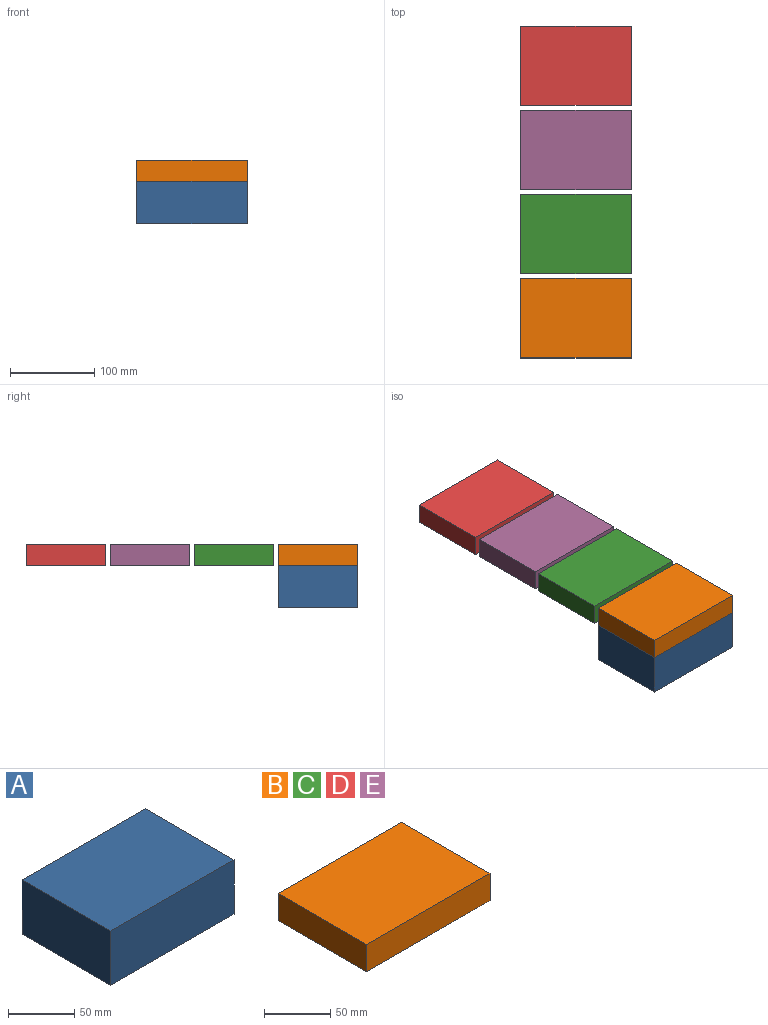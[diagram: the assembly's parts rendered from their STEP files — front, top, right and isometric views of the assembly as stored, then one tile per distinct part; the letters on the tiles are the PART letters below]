
ASSEMBLY  parts=5 mates=1
PART A: 6 faces, bbox 131.2x94.4x50 mm
  f0: plane 131.18x50mm, normal (0,-1,0), area 6559.2mm2, adj f1,f3,f4,f5
  f1: plane 94.37x50mm, normal (1,0,0), area 4718.6mm2, adj f0,f2,f4,f5
  f2: plane 131.18x50mm, normal (0,1,0), area 6559.2mm2, adj f1,f3,f4,f5
  f3: plane 94.37x50mm, normal (-1,0,0), area 4718.6mm2, adj f0,f2,f4,f5
  f4: plane 131.18x94.37mm, normal (0,0,1), area 12380.2mm2, adj f0,f1,f2,f3
  f5: plane 131.18x94.37mm, normal (0,0,-1), area 12380.2mm2, adj f0,f1,f2,f3
PART B: 6 faces, bbox 131.2x94.4x25 mm
  f0: plane 131.18x25mm, normal (0,-1,0), area 3279.6mm2, adj f1,f3,f4,f5
  f1: plane 94.37x25mm, normal (1,0,0), area 2359.3mm2, adj f0,f2,f4,f5
  f2: plane 131.18x25mm, normal (0,1,0), area 3279.6mm2, adj f1,f3,f4,f5
  f3: plane 94.37x25mm, normal (-1,0,0), area 2359.3mm2, adj f0,f2,f4,f5
  f4: plane 131.18x94.37mm, normal (0,0,1), area 12380.2mm2, adj f0,f1,f2,f3
  f5: plane 131.18x94.37mm, normal (0,0,-1), area 12380.2mm2, adj f0,f1,f2,f3
PART C: same geometry as B
PART D: same geometry as B
PART E: same geometry as B
PLACE A at identity fixed
PLACE B at identity
PLACE C t=(0,100,0)mm
PLACE D t=(0,300,0)mm
PLACE E t=(0,200,0)mm
MATE fastened B.f5 <-> A.f4  axis (0,0,-1) through (0,-4.68,50)mm
